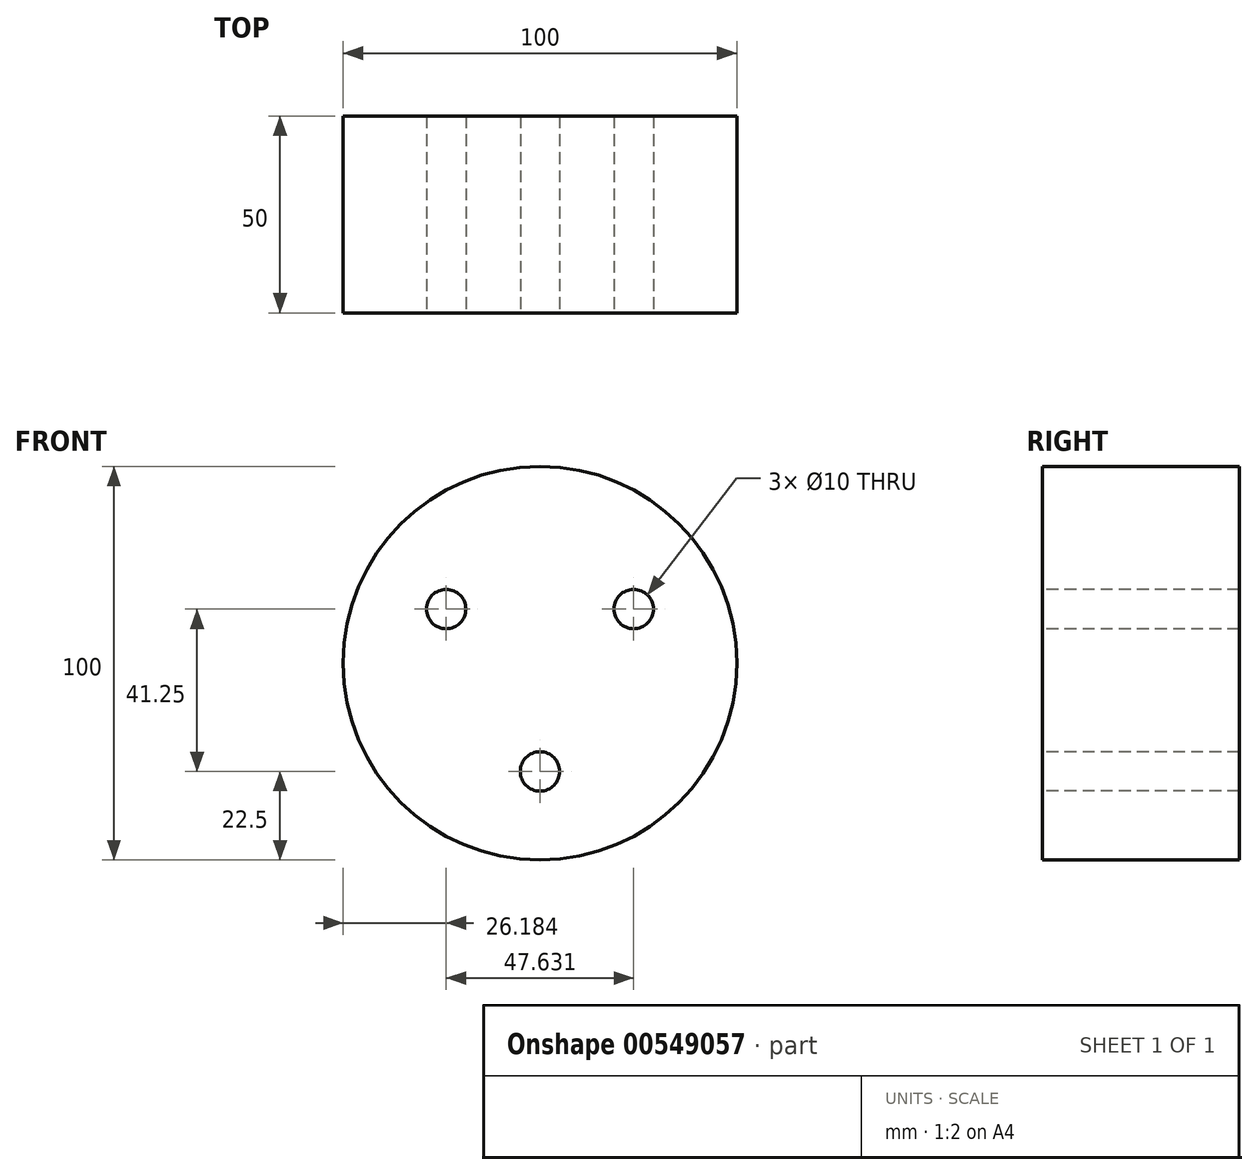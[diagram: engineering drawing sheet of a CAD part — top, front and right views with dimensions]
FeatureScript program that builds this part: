
annotation { "Feature Type Name" : "Feature", "Feature Type Description" : "" }
export const myFeature = defineFeature(function(context is Context, id is Id, definition is map)
    precondition{}
    {
        {
            var Q0;
            Q0=qCreatedBy(makeId("Front.planeOp"),FACE);
            var sketch = newSketch(context, id + "F0", { "sketchPlane" : qUnion([Q0])});
            skCircle(sketch, "E0", {"center": v(0, 0) * mm, "radius": 50 * mm});
            skSolve(sketch);
        }
        {
            var Q0;
            Q0 = qSketchRegion(id + "F0", true);
            extrude(context, id + "F1", {"entities" : qUnion([Q0]), "endBound" : BoundingType.SYMMETRIC, "depth" : 50 * mm, "offsetDistance" : 25 * mm});
        }
        {
            var Q0;
            Q0=makeQuery(id+"F1.opExtrude","CAP_FACE",FACE,{"disambiguationData":[OSD([sQuery(id+"F0.wireOp",EDGE,"E0")])],"isStart":false});
            var sketch = newSketch(context, id + "F2", { "sketchPlane" : qUnion([Q0])});
            skCircle(sketch, "E1", {"center": v(-23.82, 13.75) * mm, "radius": 5 * mm});
            skCircle(sketch, "E2", {"center": v(0, -27.5) * mm, "radius": 5 * mm});
            skCircle(sketch, "E3", {"center": v(23.82, 13.75) * mm, "radius": 5 * mm});
            skCircle(sketch, "E4", {"center": v(0, 0) * mm, "radius": 27.5 * mm, "construction": true});
            skLineSegment(sketch, "E5", {"start": v(0, 0) * mm, "end": v(-54.43, 31.42) * mm});
            skLineSegment(sketch, "E6", {"start": v(0, 0) * mm, "end": v(52.16, 30.12) * mm});
            skSolve(sketch);
        }
        {
            var Q0;
            Q0 = qSketchRegion(id + "F2", true);
            extrude(context, id + "F3", {"entities" : qUnion([Q0]), "operationType" : NewBodyOperationType.REMOVE, "oppositeDirection" : true, "depth" : 74 * mm, "offsetDistance" : 25 * mm});
        }
    });
